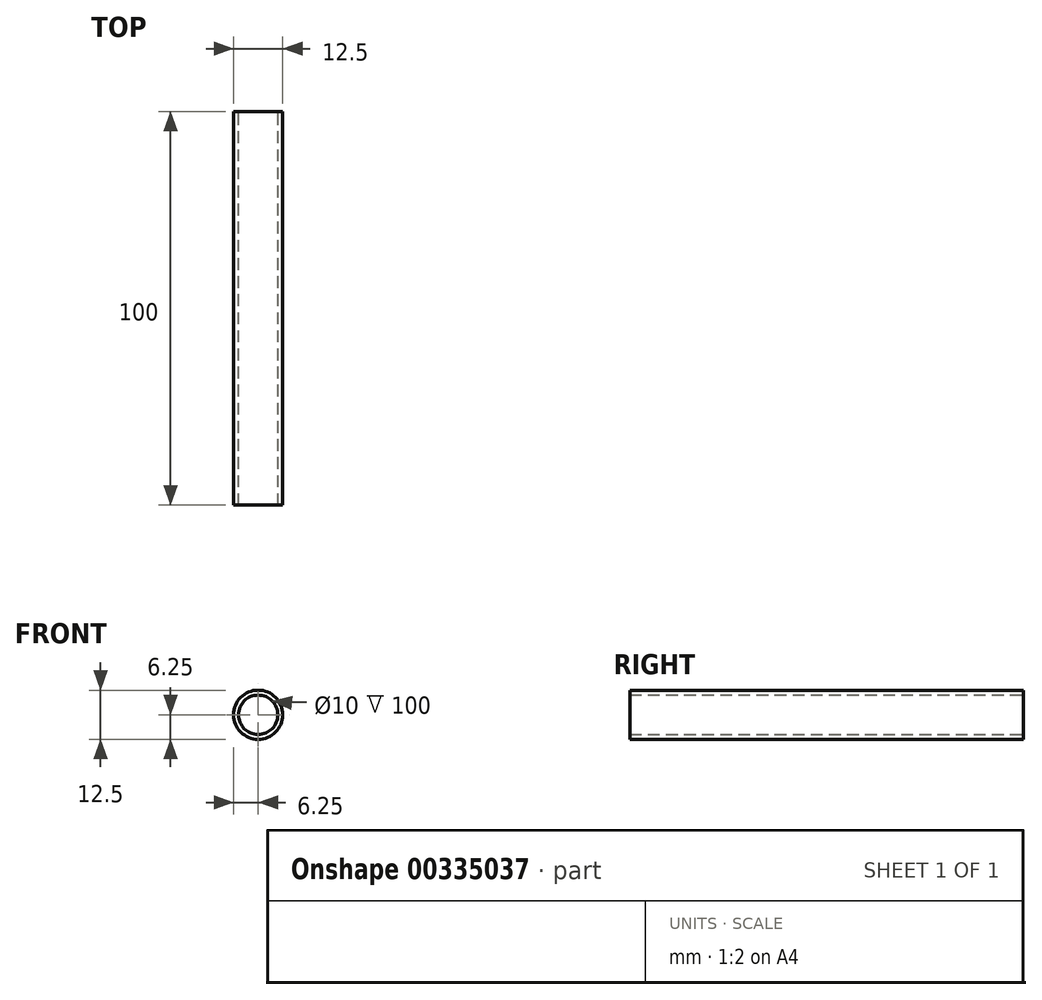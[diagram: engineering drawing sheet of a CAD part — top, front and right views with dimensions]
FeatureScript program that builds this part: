
annotation { "Feature Type Name" : "Feature", "Feature Type Description" : "" }
export const myFeature = defineFeature(function(context is Context, id is Id, definition is map)
    precondition{}
    {
        {
            var Q0;
            Q0=qCreatedBy(makeId("Front.planeOp"),FACE);
            var sketch = newSketch(context, id + "F0", { "sketchPlane" : qUnion([Q0])});
            skCircle(sketch, "E0", {"center": v(0, 0) * mm, "radius": 5 * mm});
            skCircle(sketch, "E1", {"center": v(0, 0) * mm, "radius": 6.25 * mm});
            skSolve(sketch);
        }
        {
            var Q0;
            Q0=makeQuery(id+"F0.imprint","IMPRINT",FACE,{"disambiguationData":[TD([[makeQuery(id+"F0.imprint","IMPRINT",EDGE,{"derivedFrom":sQuery(id+"F0.wireOp",EDGE,"E0")}),-1.0]])]});
            extrude(context, id + "F1", {"entities" : qUnion([Q0]), "depth" : 100 * mm});
        }
    });
